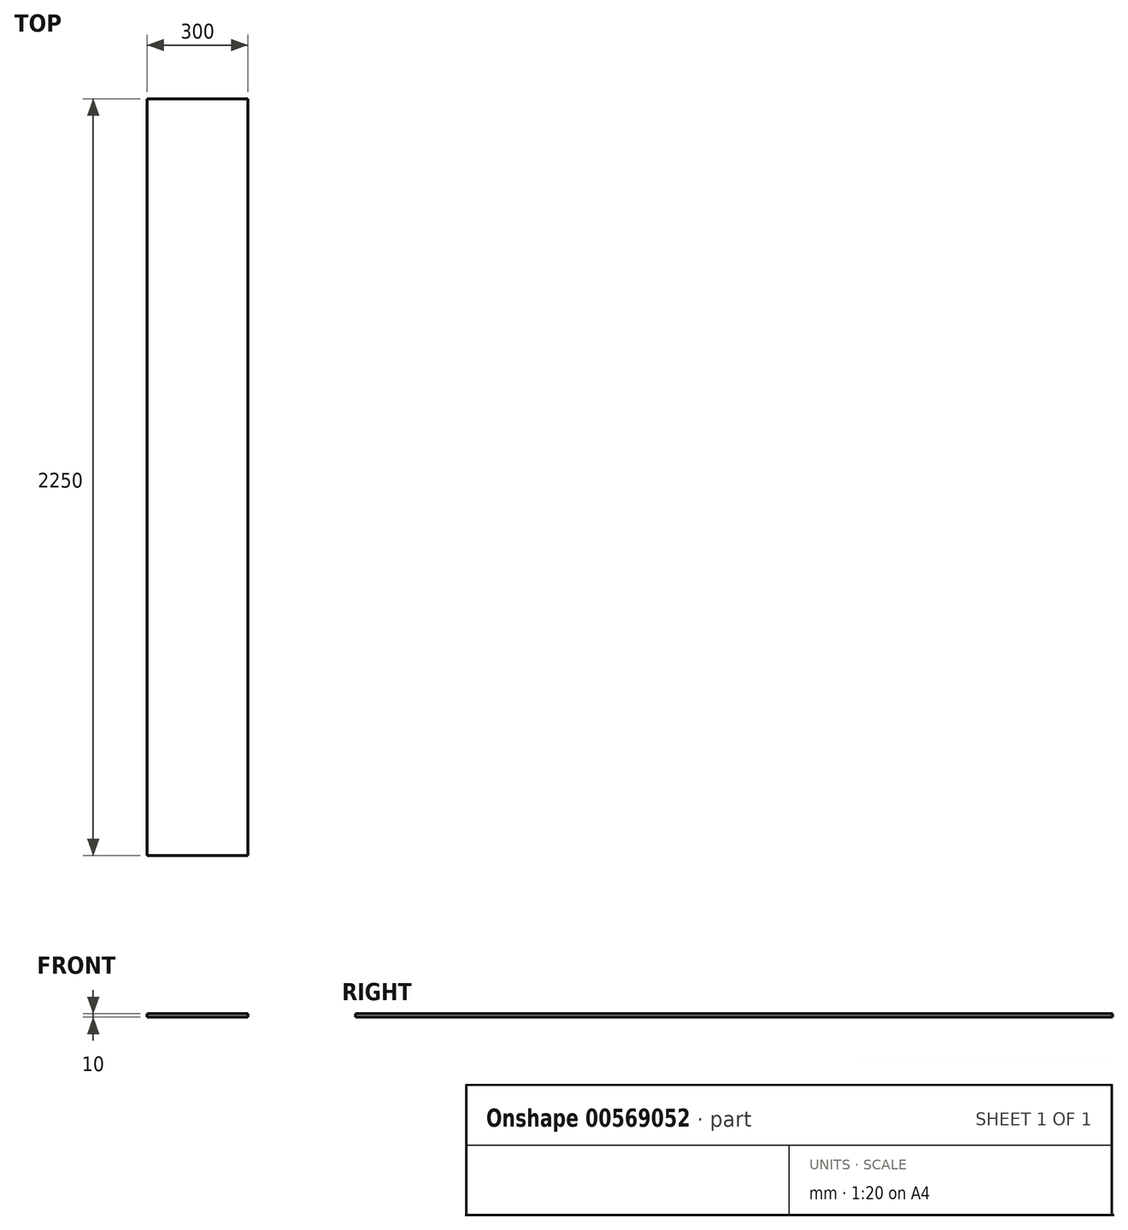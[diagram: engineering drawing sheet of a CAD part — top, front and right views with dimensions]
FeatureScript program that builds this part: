
annotation { "Feature Type Name" : "Feature", "Feature Type Description" : "" }
export const myFeature = defineFeature(function(context is Context, id is Id, definition is map)
    precondition{}
    {
        {
            var Q0;
            Q0=qCreatedBy(makeId("Top.planeOp"), FACE);
            var sketch = newSketch(context, id + "F0", { "sketchPlane" : qUnion([Q0])});
            skLineSegment(sketch, "E0.bottom", {"start": v(-203.05, 2164.97) * mm, "end": v(96.95, 2164.97) * mm});
            skLineSegment(sketch, "E0.top", {"start": v(-203.05, -85.03) * mm, "end": v(96.95, -85.03) * mm});
            skLineSegment(sketch, "E0.left", {"start": v(-203.05, 2164.97) * mm, "end": v(-203.05, -85.03) * mm});
            skLineSegment(sketch, "E0.right", {"start": v(96.95, 2164.97) * mm, "end": v(96.95, -85.03) * mm});
            skSolve(sketch);
        }
        {
            var Q0;
            Q0 = qSketchRegion(id + "F0", true);
            extrude(context, id + "F1", {"entities" : qUnion([Q0]), "depth" : 10 * mm, "offsetDistance" : 25 * mm});
        }
    });
